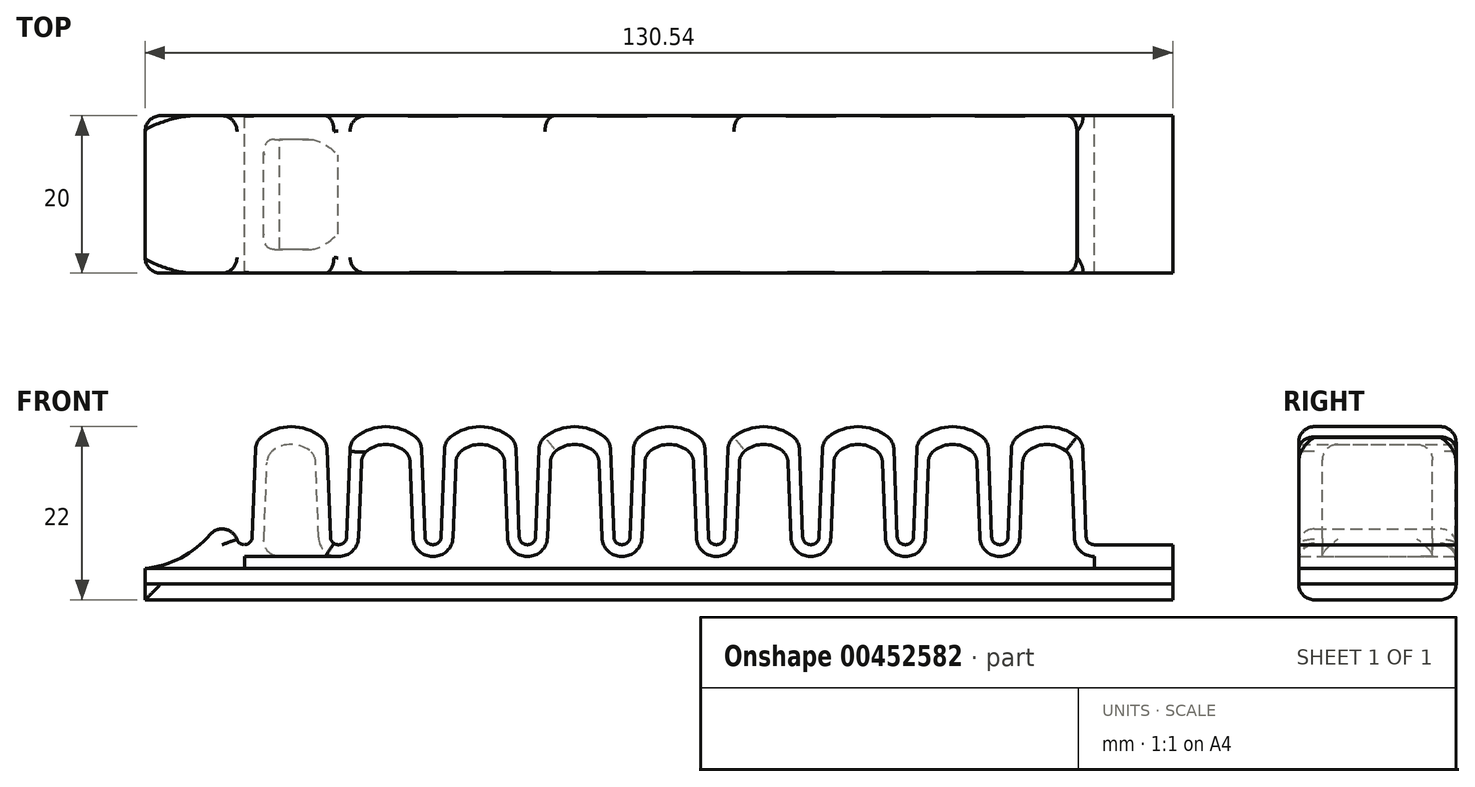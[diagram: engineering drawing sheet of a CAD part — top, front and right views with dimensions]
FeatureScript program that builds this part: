
annotation { "Feature Type Name" : "Feature", "Feature Type Description" : "" }
export const myFeature = defineFeature(function(context is Context, id is Id, definition is map)
    precondition{}
    {
        {
            assignVariable(context, id + "F0", {"name" : "vacChamberL", "anyValue" : 20});
        }
        {
            assignVariable(context, id + "F1", {"name" : "vacChamberFillet", "anyValue" : 1});
        }
        {
            assignVariable(context, id + "F2", {"name" : "vacChamberInterChamberWallThickness", "anyValue" : 1.5});
        }
        {
            var Q0;
            Q0=qCreatedBy(makeId("Front.planeOp"),FACE);
            var sketch = newSketch(context, id + "F3", { "sketchPlane" : qUnion([Q0])});
            skLineSegment(sketch, "E0", {"start": v(0, 0) * mm, "end": v(0, 5) * mm, "construction": true});
            skLineSegment(sketch, "E1", {"start": v(0, 0) * mm, "end": v(5, 0) * mm, "construction": true});
            skLineSegment(sketch, "E2", {"start": v(5, 0) * mm, "end": v(5, 20) * mm, "construction": true});
            skLineSegment(sketch, "E3", {"start": v(5, 0) * mm, "end": v(0.5, 0) * mm, "construction": true});
            skLineSegment(sketch, "E4", {"start": v(0.5, 0) * mm, "end": v(0.5, 18) * mm, "construction": true});
            skLineSegment(sketch, "E5", {"start": v(0.04, 5.96) * mm, "end": v(0.47, 17.2) * mm});
            skLineSegment(sketch, "E6", {"start": v(-0.96, 5) * mm, "end": v(-1, 5) * mm});
            skPoint(sketch, "E7.visualSharp", {"position": v(0, 5) * mm});
            skArc(sketch, "E7.filletArc", {"start": v(-0.96, 5) * mm, "mid": v(-0.27, 5.28) * mm, "end": v(0.04, 5.96) * mm});
            skArc(sketch, "E8.MirrorCS", {"start": v(10.96, 5) * mm, "mid": v(10.27, 5.28) * mm, "end": v(9.96, 5.96) * mm});
            skLineSegment(sketch, "E9.MirrorCS", {"start": v(9.96, 5.96) * mm, "end": v(9.53, 17.2) * mm});
            skArc(sketch, "E10", {"start": v(8.78, 18.68) * mm, "mid": v(5, 20) * mm, "end": v(1.22, 18.68) * mm});
            skPoint(sketch, "E11.visualSharp", {"position": v(0.5, 18) * mm});
            skArc(sketch, "E11.filletArc", {"start": v(1.22, 18.68) * mm, "mid": v(0.68, 18.02) * mm, "end": v(0.47, 17.2) * mm});
            skPoint(sketch, "E12.visualSharp", {"position": v(9.5, 18) * mm});
            skArc(sketch, "E12.filletArc", {"start": v(9.53, 17.2) * mm, "mid": v(9.32, 18.02) * mm, "end": v(8.78, 18.68) * mm});
            skSolve(sketch);
        }
        {
            var Q0;
            Q0=qCreatedBy(makeId("Front.planeOp"),FACE);
            var sketch = newSketch(context, id + "F4", { "sketchPlane" : qUnion([Q0])});
            skLineSegment(sketch, "E13.0", {"start": v(0.04, 5.96) * mm, "end": v(0.47, 17.2) * mm});
            skArc(sketch, "E13.1", {"start": v(-0.96, 5) * mm, "mid": v(-0.27, 5.28) * mm, "end": v(0.04, 5.96) * mm});
            skArc(sketch, "E13.2", {"start": v(8.78, 18.68) * mm, "mid": v(5, 20) * mm, "end": v(1.22, 18.68) * mm});
            skArc(sketch, "E13.3", {"start": v(1.22, 18.68) * mm, "mid": v(0.68, 18.02) * mm, "end": v(0.47, 17.2) * mm});
            skArc(sketch, "E13.4", {"start": v(9.53, 17.2) * mm, "mid": v(9.32, 18.02) * mm, "end": v(8.78, 18.68) * mm});
            skLineSegment(sketch, "E13.5", {"start": v(9.96, 5.96) * mm, "end": v(9.53, 17.2) * mm});
            skArc(sketch, "E13.6", {"start": v(10.96, 5) * mm, "mid": v(10.27, 5.28) * mm, "end": v(9.96, 5.96) * mm});
            skArc(sketch, "E14.1.0.0", {"start": v(22.96, 5) * mm, "mid": v(22.27, 5.28) * mm, "end": v(21.96, 5.96) * mm});
            skArc(sketch, "E14.1.0.1", {"start": v(20.78, 18.68) * mm, "mid": v(17, 20) * mm, "end": v(13.22, 18.68) * mm});
            skArc(sketch, "E14.1.0.2", {"start": v(11.04, 5) * mm, "mid": v(11.73, 5.28) * mm, "end": v(12.04, 5.96) * mm});
            skLineSegment(sketch, "E14.1.0.3", {"start": v(12.04, 5.96) * mm, "end": v(12.47, 17.2) * mm});
            skLineSegment(sketch, "E14.1.0.4", {"start": v(21.96, 5.96) * mm, "end": v(21.53, 17.2) * mm});
            skArc(sketch, "E14.1.0.5", {"start": v(21.53, 17.2) * mm, "mid": v(21.32, 18.02) * mm, "end": v(20.78, 18.68) * mm});
            skArc(sketch, "E14.1.0.6", {"start": v(13.22, 18.68) * mm, "mid": v(12.68, 18.02) * mm, "end": v(12.47, 17.2) * mm});
            skArc(sketch, "E14.2.0.0", {"start": v(34.96, 5) * mm, "mid": v(34.27, 5.28) * mm, "end": v(33.96, 5.96) * mm});
            skArc(sketch, "E14.2.0.1", {"start": v(32.78, 18.68) * mm, "mid": v(29, 20) * mm, "end": v(25.22, 18.68) * mm});
            skArc(sketch, "E14.2.0.2", {"start": v(23.04, 5) * mm, "mid": v(23.73, 5.28) * mm, "end": v(24.04, 5.96) * mm});
            skLineSegment(sketch, "E14.2.0.3", {"start": v(24.04, 5.96) * mm, "end": v(24.47, 17.2) * mm});
            skLineSegment(sketch, "E14.2.0.4", {"start": v(33.96, 5.96) * mm, "end": v(33.53, 17.2) * mm});
            skArc(sketch, "E14.2.0.5", {"start": v(33.53, 17.2) * mm, "mid": v(33.32, 18.02) * mm, "end": v(32.78, 18.68) * mm});
            skArc(sketch, "E14.2.0.6", {"start": v(25.22, 18.68) * mm, "mid": v(24.68, 18.02) * mm, "end": v(24.47, 17.2) * mm});
            skArc(sketch, "E14.3.0.0", {"start": v(46.96, 5) * mm, "mid": v(46.27, 5.28) * mm, "end": v(45.96, 5.96) * mm});
            skArc(sketch, "E14.3.0.1", {"start": v(44.78, 18.68) * mm, "mid": v(41, 20) * mm, "end": v(37.22, 18.68) * mm});
            skArc(sketch, "E14.3.0.2", {"start": v(35.04, 5) * mm, "mid": v(35.73, 5.28) * mm, "end": v(36.04, 5.96) * mm});
            skLineSegment(sketch, "E14.3.0.3", {"start": v(36.04, 5.96) * mm, "end": v(36.47, 17.2) * mm});
            skLineSegment(sketch, "E14.3.0.4", {"start": v(45.96, 5.96) * mm, "end": v(45.53, 17.2) * mm});
            skArc(sketch, "E14.3.0.5", {"start": v(45.53, 17.2) * mm, "mid": v(45.32, 18.02) * mm, "end": v(44.78, 18.68) * mm});
            skArc(sketch, "E14.3.0.6", {"start": v(37.22, 18.68) * mm, "mid": v(36.68, 18.02) * mm, "end": v(36.47, 17.2) * mm});
            skArc(sketch, "E14.4.0.0", {"start": v(58.96, 5) * mm, "mid": v(58.27, 5.28) * mm, "end": v(57.96, 5.96) * mm});
            skArc(sketch, "E14.4.0.1", {"start": v(56.78, 18.68) * mm, "mid": v(53, 20) * mm, "end": v(49.22, 18.68) * mm});
            skArc(sketch, "E14.4.0.2", {"start": v(47.04, 5) * mm, "mid": v(47.73, 5.28) * mm, "end": v(48.04, 5.96) * mm});
            skLineSegment(sketch, "E14.4.0.3", {"start": v(48.04, 5.96) * mm, "end": v(48.47, 17.2) * mm});
            skLineSegment(sketch, "E14.4.0.4", {"start": v(57.96, 5.96) * mm, "end": v(57.53, 17.2) * mm});
            skArc(sketch, "E14.4.0.5", {"start": v(57.53, 17.2) * mm, "mid": v(57.32, 18.02) * mm, "end": v(56.78, 18.68) * mm});
            skArc(sketch, "E14.4.0.6", {"start": v(49.22, 18.68) * mm, "mid": v(48.68, 18.02) * mm, "end": v(48.47, 17.2) * mm});
            skArc(sketch, "E14.5.0.0", {"start": v(70.96, 5) * mm, "mid": v(70.27, 5.28) * mm, "end": v(69.96, 5.96) * mm});
            skArc(sketch, "E14.5.0.1", {"start": v(68.78, 18.68) * mm, "mid": v(65, 20) * mm, "end": v(61.22, 18.68) * mm});
            skArc(sketch, "E14.5.0.2", {"start": v(59.04, 5) * mm, "mid": v(59.73, 5.28) * mm, "end": v(60.04, 5.96) * mm});
            skLineSegment(sketch, "E14.5.0.3", {"start": v(60.04, 5.96) * mm, "end": v(60.47, 17.2) * mm});
            skLineSegment(sketch, "E14.5.0.4", {"start": v(69.96, 5.96) * mm, "end": v(69.53, 17.2) * mm});
            skArc(sketch, "E14.5.0.5", {"start": v(69.53, 17.2) * mm, "mid": v(69.32, 18.02) * mm, "end": v(68.78, 18.68) * mm});
            skArc(sketch, "E14.5.0.6", {"start": v(61.22, 18.68) * mm, "mid": v(60.68, 18.02) * mm, "end": v(60.47, 17.2) * mm});
            skArc(sketch, "E14.6.0.0", {"start": v(82.96, 5) * mm, "mid": v(82.27, 5.28) * mm, "end": v(81.96, 5.96) * mm});
            skArc(sketch, "E14.6.0.1", {"start": v(80.78, 18.68) * mm, "mid": v(77, 20) * mm, "end": v(73.22, 18.68) * mm});
            skArc(sketch, "E14.6.0.2", {"start": v(71.04, 5) * mm, "mid": v(71.73, 5.28) * mm, "end": v(72.04, 5.96) * mm});
            skLineSegment(sketch, "E14.6.0.3", {"start": v(72.04, 5.96) * mm, "end": v(72.47, 17.2) * mm});
            skLineSegment(sketch, "E14.6.0.4", {"start": v(81.96, 5.96) * mm, "end": v(81.53, 17.2) * mm});
            skArc(sketch, "E14.6.0.5", {"start": v(81.53, 17.2) * mm, "mid": v(81.32, 18.02) * mm, "end": v(80.78, 18.68) * mm});
            skArc(sketch, "E14.6.0.6", {"start": v(73.22, 18.68) * mm, "mid": v(72.68, 18.02) * mm, "end": v(72.47, 17.2) * mm});
            skArc(sketch, "E14.7.0.0", {"start": v(94.96, 5) * mm, "mid": v(94.27, 5.28) * mm, "end": v(93.96, 5.96) * mm});
            skArc(sketch, "E14.7.0.1", {"start": v(92.78, 18.68) * mm, "mid": v(89, 20) * mm, "end": v(85.22, 18.68) * mm});
            skArc(sketch, "E14.7.0.2", {"start": v(83.04, 5) * mm, "mid": v(83.73, 5.28) * mm, "end": v(84.04, 5.96) * mm});
            skLineSegment(sketch, "E14.7.0.3", {"start": v(84.04, 5.96) * mm, "end": v(84.47, 17.2) * mm});
            skLineSegment(sketch, "E14.7.0.4", {"start": v(93.96, 5.96) * mm, "end": v(93.53, 17.2) * mm});
            skArc(sketch, "E14.7.0.5", {"start": v(93.53, 17.2) * mm, "mid": v(93.32, 18.02) * mm, "end": v(92.78, 18.68) * mm});
            skArc(sketch, "E14.7.0.6", {"start": v(85.22, 18.68) * mm, "mid": v(84.68, 18.02) * mm, "end": v(84.47, 17.2) * mm});
            skLineSegment(sketch, "E14.direction1", {"start": v(-0.96, 5) * mm, "end": v(11.04, 5) * mm, "construction": true});
            skLineSegment(sketch, "E15", {"start": v(-0.96, 5) * mm, "end": v(-0.96, 2.72) * mm, "construction": true});
            skArc(sketch, "E16.MirrorCS", {"start": v(-0.96, 5) * mm, "mid": v(-1.66, 5.28) * mm, "end": v(-1.96, 5.96) * mm});
            skLineSegment(sketch, "E17", {"start": v(-1.96, 5.96) * mm, "end": v(-2.08, 8.96) * mm});
            skLineSegment(sketch, "E18", {"start": v(-2.08, 8.96) * mm, "end": v(-3.58, 8.96) * mm});
            skLineSegment(sketch, "E19", {"start": v(-3.58, 0) * mm, "end": v(-13.58, 0) * mm, "construction": true});
            skLineSegment(sketch, "E20", {"start": v(-3.58, 0) * mm, "end": v(-5.58, 0) * mm, "construction": true});
            skLineSegment(sketch, "E21", {"start": v(-5.58, 0) * mm, "end": v(-5.58, 6) * mm, "construction": true});
            skLineSegment(sketch, "E22", {"start": v(10.96, 5) * mm, "end": v(11.04, 5) * mm});
            skLineSegment(sketch, "E23", {"start": v(22.96, 5) * mm, "end": v(23.04, 5) * mm});
            skLineSegment(sketch, "E24", {"start": v(34.96, 5) * mm, "end": v(35.04, 5) * mm});
            skLineSegment(sketch, "E25", {"start": v(46.96, 5) * mm, "end": v(47.04, 5) * mm});
            skLineSegment(sketch, "E26", {"start": v(58.96, 5) * mm, "end": v(59.04, 5) * mm});
            skLineSegment(sketch, "E27", {"start": v(70.96, 5) * mm, "end": v(71.04, 5) * mm});
            skLineSegment(sketch, "E28", {"start": v(82.96, 5) * mm, "end": v(83.04, 5) * mm});
            skArc(sketch, "E29.0.8.0", {"start": v(106.96, 5) * mm, "mid": v(106.27, 5.28) * mm, "end": v(105.96, 5.96) * mm});
            skArc(sketch, "E29.4.8.0", {"start": v(104.78, 18.68) * mm, "mid": v(101, 20) * mm, "end": v(97.22, 18.68) * mm});
            skArc(sketch, "E29.8.8.0", {"start": v(95.04, 5) * mm, "mid": v(95.73, 5.28) * mm, "end": v(96.04, 5.96) * mm});
            skLineSegment(sketch, "E29.12.8.0", {"start": v(96.04, 5.96) * mm, "end": v(96.47, 17.2) * mm});
            skLineSegment(sketch, "E29.15.8.0", {"start": v(105.96, 5.96) * mm, "end": v(105.53, 17.2) * mm});
            skArc(sketch, "E29.18.8.0", {"start": v(105.53, 17.2) * mm, "mid": v(105.32, 18.02) * mm, "end": v(104.78, 18.68) * mm});
            skArc(sketch, "E29.22.8.0", {"start": v(97.22, 18.68) * mm, "mid": v(96.68, 18.02) * mm, "end": v(96.47, 17.2) * mm});
            skLineSegment(sketch, "E30", {"start": v(94.96, 5) * mm, "end": v(95.04, 5) * mm});
            skLineSegment(sketch, "E31", {"start": v(106.96, 5) * mm, "end": v(116.96, 5) * mm});
            skArc(sketch, "E32.0", {"start": v(-0.96, 3.5) * mm, "mid": v(0.77, 4.2) * mm, "end": v(1.54, 5.9) * mm});
            skLineSegment(sketch, "E32.1", {"start": v(1.54, 5.9) * mm, "end": v(1.9, 15.46) * mm});
            skLineSegment(sketch, "E32.4", {"start": v(10.96, 3.5) * mm, "end": v(11.04, 3.5) * mm});
            skArc(sketch, "E32.5", {"start": v(10.96, 3.5) * mm, "mid": v(9.23, 4.2) * mm, "end": v(8.46, 5.9) * mm});
            skLineSegment(sketch, "E32.6", {"start": v(8.46, 5.9) * mm, "end": v(8.1, 15.46) * mm});
            skArc(sketch, "E33.0", {"start": v(7.31, 16.97) * mm, "mid": v(5, 17.75) * mm, "end": v(2.69, 16.97) * mm});
            skPoint(sketch, "E34.visualSharp", {"position": v(1.93, 16.2) * mm});
            skArc(sketch, "E34.filletArc", {"start": v(2.69, 16.97) * mm, "mid": v(2.13, 16.3) * mm, "end": v(1.9, 15.46) * mm});
            skPoint(sketch, "E35.visualSharp", {"position": v(8.07, 16.2) * mm});
            skArc(sketch, "E35.filletArc", {"start": v(8.1, 15.46) * mm, "mid": v(7.87, 16.3) * mm, "end": v(7.31, 16.97) * mm});
            skArc(sketch, "E36.1.0.0", {"start": v(22.96, 3.5) * mm, "mid": v(21.23, 4.2) * mm, "end": v(20.46, 5.9) * mm});
            skLineSegment(sketch, "E36.1.0.1", {"start": v(22.96, 3.5) * mm, "end": v(23.04, 3.5) * mm});
            skLineSegment(sketch, "E36.1.0.2", {"start": v(20.46, 5.9) * mm, "end": v(20.1, 15.46) * mm});
            skArc(sketch, "E36.1.0.3", {"start": v(20.1, 15.46) * mm, "mid": v(19.87, 16.3) * mm, "end": v(19.31, 16.97) * mm});
            skArc(sketch, "E36.1.0.4", {"start": v(19.31, 16.97) * mm, "mid": v(17, 17.75) * mm, "end": v(14.69, 16.97) * mm});
            skArc(sketch, "E36.1.0.5", {"start": v(14.69, 16.97) * mm, "mid": v(14.13, 16.3) * mm, "end": v(13.9, 15.46) * mm});
            skLineSegment(sketch, "E36.1.0.6", {"start": v(13.54, 5.9) * mm, "end": v(13.9, 15.46) * mm});
            skArc(sketch, "E36.1.0.7", {"start": v(11.04, 3.5) * mm, "mid": v(12.77, 4.2) * mm, "end": v(13.54, 5.9) * mm});
            skArc(sketch, "E36.2.0.0", {"start": v(34.96, 3.5) * mm, "mid": v(33.23, 4.2) * mm, "end": v(32.46, 5.9) * mm});
            skLineSegment(sketch, "E36.2.0.1", {"start": v(34.96, 3.5) * mm, "end": v(35.04, 3.5) * mm});
            skLineSegment(sketch, "E36.2.0.2", {"start": v(32.46, 5.9) * mm, "end": v(32.1, 15.46) * mm});
            skArc(sketch, "E36.2.0.3", {"start": v(32.1, 15.46) * mm, "mid": v(31.87, 16.3) * mm, "end": v(31.31, 16.97) * mm});
            skArc(sketch, "E36.2.0.4", {"start": v(31.31, 16.97) * mm, "mid": v(29, 17.75) * mm, "end": v(26.69, 16.97) * mm});
            skArc(sketch, "E36.2.0.5", {"start": v(26.69, 16.97) * mm, "mid": v(26.13, 16.3) * mm, "end": v(25.9, 15.46) * mm});
            skLineSegment(sketch, "E36.2.0.6", {"start": v(25.54, 5.9) * mm, "end": v(25.9, 15.46) * mm});
            skArc(sketch, "E36.2.0.7", {"start": v(23.04, 3.5) * mm, "mid": v(24.77, 4.2) * mm, "end": v(25.54, 5.9) * mm});
            skArc(sketch, "E36.3.0.0", {"start": v(46.96, 3.5) * mm, "mid": v(45.23, 4.2) * mm, "end": v(44.46, 5.9) * mm});
            skLineSegment(sketch, "E36.3.0.1", {"start": v(46.96, 3.5) * mm, "end": v(47.04, 3.5) * mm});
            skLineSegment(sketch, "E36.3.0.2", {"start": v(44.46, 5.9) * mm, "end": v(44.1, 15.46) * mm});
            skArc(sketch, "E36.3.0.3", {"start": v(44.1, 15.46) * mm, "mid": v(43.87, 16.3) * mm, "end": v(43.31, 16.97) * mm});
            skArc(sketch, "E36.3.0.4", {"start": v(43.31, 16.97) * mm, "mid": v(41, 17.75) * mm, "end": v(38.69, 16.97) * mm});
            skArc(sketch, "E36.3.0.5", {"start": v(38.69, 16.97) * mm, "mid": v(38.13, 16.3) * mm, "end": v(37.9, 15.46) * mm});
            skLineSegment(sketch, "E36.3.0.6", {"start": v(37.54, 5.9) * mm, "end": v(37.9, 15.46) * mm});
            skArc(sketch, "E36.3.0.7", {"start": v(35.04, 3.5) * mm, "mid": v(36.77, 4.2) * mm, "end": v(37.54, 5.9) * mm});
            skArc(sketch, "E36.4.0.0", {"start": v(58.96, 3.5) * mm, "mid": v(57.23, 4.2) * mm, "end": v(56.46, 5.9) * mm});
            skLineSegment(sketch, "E36.4.0.1", {"start": v(58.96, 3.5) * mm, "end": v(59.04, 3.5) * mm});
            skLineSegment(sketch, "E36.4.0.2", {"start": v(56.46, 5.9) * mm, "end": v(56.1, 15.46) * mm});
            skArc(sketch, "E36.4.0.3", {"start": v(56.1, 15.46) * mm, "mid": v(55.87, 16.3) * mm, "end": v(55.31, 16.97) * mm});
            skArc(sketch, "E36.4.0.4", {"start": v(55.31, 16.97) * mm, "mid": v(53, 17.75) * mm, "end": v(50.69, 16.97) * mm});
            skArc(sketch, "E36.4.0.5", {"start": v(50.69, 16.97) * mm, "mid": v(50.13, 16.3) * mm, "end": v(49.9, 15.46) * mm});
            skLineSegment(sketch, "E36.4.0.6", {"start": v(49.54, 5.9) * mm, "end": v(49.9, 15.46) * mm});
            skArc(sketch, "E36.4.0.7", {"start": v(47.04, 3.5) * mm, "mid": v(48.77, 4.2) * mm, "end": v(49.54, 5.9) * mm});
            skArc(sketch, "E36.5.0.0", {"start": v(70.96, 3.5) * mm, "mid": v(69.23, 4.2) * mm, "end": v(68.46, 5.9) * mm});
            skLineSegment(sketch, "E36.5.0.1", {"start": v(70.96, 3.5) * mm, "end": v(71.04, 3.5) * mm});
            skLineSegment(sketch, "E36.5.0.2", {"start": v(68.46, 5.9) * mm, "end": v(68.1, 15.46) * mm});
            skArc(sketch, "E36.5.0.3", {"start": v(68.1, 15.46) * mm, "mid": v(67.87, 16.3) * mm, "end": v(67.31, 16.97) * mm});
            skArc(sketch, "E36.5.0.4", {"start": v(67.31, 16.97) * mm, "mid": v(65, 17.75) * mm, "end": v(62.69, 16.97) * mm});
            skArc(sketch, "E36.5.0.5", {"start": v(62.69, 16.97) * mm, "mid": v(62.13, 16.3) * mm, "end": v(61.9, 15.46) * mm});
            skLineSegment(sketch, "E36.5.0.6", {"start": v(61.54, 5.9) * mm, "end": v(61.9, 15.46) * mm});
            skArc(sketch, "E36.5.0.7", {"start": v(59.04, 3.5) * mm, "mid": v(60.77, 4.2) * mm, "end": v(61.54, 5.9) * mm});
            skArc(sketch, "E36.6.0.0", {"start": v(82.96, 3.5) * mm, "mid": v(81.23, 4.2) * mm, "end": v(80.46, 5.9) * mm});
            skLineSegment(sketch, "E36.6.0.1", {"start": v(82.96, 3.5) * mm, "end": v(83.04, 3.5) * mm});
            skLineSegment(sketch, "E36.6.0.2", {"start": v(80.46, 5.9) * mm, "end": v(80.1, 15.46) * mm});
            skArc(sketch, "E36.6.0.3", {"start": v(80.1, 15.46) * mm, "mid": v(79.87, 16.3) * mm, "end": v(79.31, 16.97) * mm});
            skArc(sketch, "E36.6.0.4", {"start": v(79.31, 16.97) * mm, "mid": v(77, 17.75) * mm, "end": v(74.69, 16.97) * mm});
            skArc(sketch, "E36.6.0.5", {"start": v(74.69, 16.97) * mm, "mid": v(74.13, 16.3) * mm, "end": v(73.9, 15.46) * mm});
            skLineSegment(sketch, "E36.6.0.6", {"start": v(73.54, 5.9) * mm, "end": v(73.9, 15.46) * mm});
            skArc(sketch, "E36.6.0.7", {"start": v(71.04, 3.5) * mm, "mid": v(72.77, 4.2) * mm, "end": v(73.54, 5.9) * mm});
            skArc(sketch, "E36.7.0.0", {"start": v(94.96, 3.5) * mm, "mid": v(93.23, 4.2) * mm, "end": v(92.46, 5.9) * mm});
            skLineSegment(sketch, "E36.7.0.1", {"start": v(94.96, 3.5) * mm, "end": v(95.04, 3.5) * mm});
            skLineSegment(sketch, "E36.7.0.2", {"start": v(92.46, 5.9) * mm, "end": v(92.1, 15.46) * mm});
            skArc(sketch, "E36.7.0.3", {"start": v(92.1, 15.46) * mm, "mid": v(91.87, 16.3) * mm, "end": v(91.31, 16.97) * mm});
            skArc(sketch, "E36.7.0.4", {"start": v(91.31, 16.97) * mm, "mid": v(89, 17.75) * mm, "end": v(86.69, 16.97) * mm});
            skArc(sketch, "E36.7.0.5", {"start": v(86.69, 16.97) * mm, "mid": v(86.13, 16.3) * mm, "end": v(85.9, 15.46) * mm});
            skLineSegment(sketch, "E36.7.0.6", {"start": v(85.54, 5.9) * mm, "end": v(85.9, 15.46) * mm});
            skArc(sketch, "E36.7.0.7", {"start": v(83.04, 3.5) * mm, "mid": v(84.77, 4.2) * mm, "end": v(85.54, 5.9) * mm});
            skArc(sketch, "E36.8.0.0", {"start": v(106.96, 3.5) * mm, "mid": v(105.23, 4.2) * mm, "end": v(104.46, 5.9) * mm});
            skLineSegment(sketch, "E36.8.0.1", {"start": v(106.96, 3.5) * mm, "end": v(107.04, 3.5) * mm});
            skLineSegment(sketch, "E36.8.0.2", {"start": v(104.46, 5.9) * mm, "end": v(104.1, 15.46) * mm});
            skArc(sketch, "E36.8.0.3", {"start": v(104.1, 15.46) * mm, "mid": v(103.87, 16.3) * mm, "end": v(103.31, 16.97) * mm});
            skArc(sketch, "E36.8.0.4", {"start": v(103.31, 16.97) * mm, "mid": v(101, 17.75) * mm, "end": v(98.69, 16.97) * mm});
            skArc(sketch, "E36.8.0.5", {"start": v(98.69, 16.97) * mm, "mid": v(98.13, 16.3) * mm, "end": v(97.9, 15.46) * mm});
            skLineSegment(sketch, "E36.8.0.6", {"start": v(97.54, 5.9) * mm, "end": v(97.9, 15.46) * mm});
            skArc(sketch, "E36.8.0.7", {"start": v(95.04, 3.5) * mm, "mid": v(96.77, 4.2) * mm, "end": v(97.54, 5.9) * mm});
            skLineSegment(sketch, "E36.direction1", {"start": v(-0.96, 3.5) * mm, "end": v(11.04, 3.5) * mm, "construction": true});
            skLineSegment(sketch, "E37", {"start": v(107.04, 3.5) * mm, "end": v(116.96, 3.5) * mm});
            skLineSegment(sketch, "E38", {"start": v(-13.58, 0) * mm, "end": v(116.96, 0) * mm});
            skLineSegment(sketch, "E39", {"start": v(116.96, 0) * mm, "end": v(116.96, 2) * mm});
            skLineSegment(sketch, "E40", {"start": v(116.96, 2) * mm, "end": v(-0.96, 2) * mm});
            skLineSegment(sketch, "E41", {"start": v(-0.96, 2) * mm, "end": v(-0.96, 3.5) * mm});
            skLineSegment(sketch, "E42", {"start": v(116.96, 3.5) * mm, "end": v(116.96, 5) * mm});
            skLineSegment(sketch, "E43", {"start": v(116.96, 3.5) * mm, "end": v(116.96, 2) * mm});
            skLineSegment(sketch, "E44", {"start": v(116.96, 0) * mm, "end": v(116.96, -2) * mm});
            skLineSegment(sketch, "E45", {"start": v(116.96, -2) * mm, "end": v(-13.58, -2) * mm});
            skLineSegment(sketch, "E46", {"start": v(-13.58, -2) * mm, "end": v(-13.58, 0) * mm});
            skLineSegment(sketch, "E47", {"start": v(-13.58, 0) * mm, "end": v(-13.58, 2) * mm});
            skLineSegment(sketch, "E48", {"start": v(-13.58, 2) * mm, "end": v(-0.96, 2) * mm});
            skArc(sketch, "E49", {"start": v(-13.58, 2) * mm, "mid": v(-7.66, 4.17) * mm, "end": v(-3.58, 8.96) * mm});
            skLineSegment(sketch, "E50", {"start": v(107.04, 3.5) * mm, "end": v(-0.96, 3.5) * mm});
            skLineSegment(sketch, "E51.0", {"start": v(109.37, 6.5) * mm, "end": v(116.96, 6.5) * mm});
            skLineSegment(sketch, "E51.1", {"start": v(107.37, 8.42) * mm, "end": v(107.1, 15.45) * mm});
            skLineSegment(sketch, "E52", {"start": v(116.96, 6.5) * mm, "end": v(116.96, 5) * mm});
            skLineSegment(sketch, "E53", {"start": v(106.02, 17.64) * mm, "end": v(104.78, 18.68) * mm});
            skPoint(sketch, "E54.visualSharp", {"position": v(107.44, 6.5) * mm});
            skArc(sketch, "E54.filletArc", {"start": v(107.37, 8.42) * mm, "mid": v(107.98, 7.06) * mm, "end": v(109.37, 6.5) * mm});
            skPoint(sketch, "E55.visualSharp", {"position": v(107.05, 16.79) * mm});
            skArc(sketch, "E55.filletArc", {"start": v(107.1, 15.45) * mm, "mid": v(106.8, 16.66) * mm, "end": v(106.02, 17.64) * mm});
            skLineSegment(sketch, "E56", {"start": v(107.04, 3.5) * mm, "end": v(107.04, 2) * mm});
            skSolve(sketch);
        }
        {
            var Q0;
            Q0=makeQuery(id+"F4.imprint","IMPRINT",FACE,{"disambiguationData":[TD([[makeQuery(id+"F4.imprint","IMPRINT",EDGE,{"derivedFrom":sQuery(id+"F4.wireOp",EDGE,"E32.0")}),-1.0]])]});
            var Q1;
            {var subQ0=sQuery(id+"F4.wireOp",EDGE,"E36.1.0.0");Q1=makeQuery(id+"F4.imprint","IMPRINT",FACE,{"disambiguationData":[TD([[makeQuery(id+"F4.imprint","IMPRINT",EDGE,{"derivedFrom":subQ0}),1.0]])]});}
            var Q2;
            {var subQ0=sQuery(id+"F4.wireOp",EDGE,"E36.2.0.0");Q2=makeQuery(id+"F4.imprint","IMPRINT",FACE,{"disambiguationData":[TD([[makeQuery(id+"F4.imprint","IMPRINT",EDGE,{"derivedFrom":subQ0}),1.0]])]});}
            var Q3;
            {var subQ0=sQuery(id+"F4.wireOp",EDGE,"E36.3.0.0");Q3=makeQuery(id+"F4.imprint","IMPRINT",FACE,{"disambiguationData":[TD([[makeQuery(id+"F4.imprint","IMPRINT",EDGE,{"derivedFrom":subQ0}),1.0]])]});}
            var Q4;
            {var subQ1=sQuery(id+"F4.wireOp",EDGE,"E36.4.0.0");Q4=makeQuery(id+"F4.imprint","IMPRINT",FACE,{"disambiguationData":[TD([[makeQuery(id+"F4.imprint","IMPRINT",EDGE,{"derivedFrom":subQ1}),1.0]])]});}
            var Q5;
            {var subQ0=sQuery(id+"F4.wireOp",EDGE,"E36.5.0.0");Q5=makeQuery(id+"F4.imprint","IMPRINT",FACE,{"disambiguationData":[TD([[makeQuery(id+"F4.imprint","IMPRINT",EDGE,{"derivedFrom":subQ0}),1.0]])]});}
            var Q6;
            {var subQ0=sQuery(id+"F4.wireOp",EDGE,"E36.6.0.0");Q6=makeQuery(id+"F4.imprint","IMPRINT",FACE,{"disambiguationData":[TD([[makeQuery(id+"F4.imprint","IMPRINT",EDGE,{"derivedFrom":subQ0}),1.0]])]});}
            var Q7;
            {var subQ0=sQuery(id+"F4.wireOp",EDGE,"E36.7.0.0");Q7=makeQuery(id+"F4.imprint","IMPRINT",FACE,{"disambiguationData":[TD([[makeQuery(id+"F4.imprint","IMPRINT",EDGE,{"derivedFrom":subQ0}),1.0]])]});}
            var Q8;
            {var subQ0=sQuery(id+"F4.wireOp",EDGE,"E36.8.0.0");Q8=makeQuery(id+"F4.imprint","IMPRINT",FACE,{"disambiguationData":[TD([[makeQuery(id+"F4.imprint","IMPRINT",EDGE,{"derivedFrom":subQ0}),1.0]])]});}
            var Q9;
            {var subQ10=sQuery(id+"F4.wireOp",EDGE,"E41");Q9=makeQuery(id+"F4.imprint","IMPRINT",FACE,{"disambiguationData":[TD([[makeQuery(id+"F4.imprint","IMPRINT",EDGE,{"derivedFrom":subQ10}),-1.0]])]});}
            extrude(context, id + "F5", {"entities" : qUnion([Q0, Q1, Q2, Q3, Q4, Q5, Q6, Q7, Q8, Q9]), "depth" : (getVariable(context, 'vacChamberL') - 4 * getVariable(context, 'vacChamberInterChamberWallThickness')) * mm, "symmetric" : true});
        }
        {
            var Q0;
            Q0=makeQuery(id+"F5.opExtrude","CAP_EDGE",EDGE,{"disambiguationData":[OSD([sQuery(id+"F4.wireOp",EDGE,"E33.0")])],"isStart":false});
            var Q1;
            Q1=makeQuery(id+"F5.opExtrude","CAP_EDGE",EDGE,{"disambiguationData":[OSD([sQuery(id+"F4.wireOp",EDGE,"E33.0")])],"isStart":true});
            var Q2;
            Q2=makeQuery(id+"F5.opExtrude","SWEPT_EDGE",EDGE,{"disambiguationData":[OSD([sQuery(id+"F4.wireOp",EDGE,"E32.0"),sQuery(id+"F4.wireOp",EDGE,"E41")])]});
            fillet(context, id + "F6", {"entities" : qUnion([Q0, Q1, Q2]), "radius" : (getVariable(context, 'vacChamberFillet') * 2) * mm, "tangentPropagation" : true, "allowEdgeOverflow" : false});
        }
        {
            var Q0;
            Q0=makeQuery(id+"F4.imprint","IMPRINT",FACE,{"disambiguationData":[TD([[makeQuery(id+"F4.imprint","IMPRINT",EDGE,{"derivedFrom":sQuery(id+"F4.wireOp",EDGE,"E13.0")}),-1.0]])]});
            var Q1;
            Q1=makeQuery(id+"F4.imprint","IMPRINT",FACE,{"disambiguationData":[TD([[makeQuery(id+"F4.imprint","IMPRINT",EDGE,{"derivedFrom":sQuery(id+"F4.wireOp",EDGE,"E32.0")}),-1.0]])]});
            var Q2;
            {var subQ6=sQuery(id+"F4.wireOp",EDGE,"E37");Q2=makeQuery(id+"F4.imprint","IMPRINT",FACE,{"disambiguationData":[TD([[makeQuery(id+"F4.imprint","IMPRINT",EDGE,{"derivedFrom":subQ6}),-1.0]])]});}
            var Q3;
            {var subQ0=sQuery(id+"F4.wireOp",EDGE,"E36.1.0.0");Q3=makeQuery(id+"F4.imprint","IMPRINT",FACE,{"disambiguationData":[TD([[makeQuery(id+"F4.imprint","IMPRINT",EDGE,{"derivedFrom":subQ0}),1.0]])]});}
            var Q4;
            {var subQ0=sQuery(id+"F4.wireOp",EDGE,"E36.2.0.0");Q4=makeQuery(id+"F4.imprint","IMPRINT",FACE,{"disambiguationData":[TD([[makeQuery(id+"F4.imprint","IMPRINT",EDGE,{"derivedFrom":subQ0}),1.0]])]});}
            var Q5;
            {var subQ0=sQuery(id+"F4.wireOp",EDGE,"E36.3.0.0");Q5=makeQuery(id+"F4.imprint","IMPRINT",FACE,{"disambiguationData":[TD([[makeQuery(id+"F4.imprint","IMPRINT",EDGE,{"derivedFrom":subQ0}),1.0]])]});}
            var Q6;
            {var subQ1=sQuery(id+"F4.wireOp",EDGE,"E36.4.0.0");Q6=makeQuery(id+"F4.imprint","IMPRINT",FACE,{"disambiguationData":[TD([[makeQuery(id+"F4.imprint","IMPRINT",EDGE,{"derivedFrom":subQ1}),1.0]])]});}
            var Q7;
            {var subQ0=sQuery(id+"F4.wireOp",EDGE,"E36.5.0.0");Q7=makeQuery(id+"F4.imprint","IMPRINT",FACE,{"disambiguationData":[TD([[makeQuery(id+"F4.imprint","IMPRINT",EDGE,{"derivedFrom":subQ0}),1.0]])]});}
            var Q8;
            {var subQ0=sQuery(id+"F4.wireOp",EDGE,"E36.6.0.0");Q8=makeQuery(id+"F4.imprint","IMPRINT",FACE,{"disambiguationData":[TD([[makeQuery(id+"F4.imprint","IMPRINT",EDGE,{"derivedFrom":subQ0}),1.0]])]});}
            var Q9;
            {var subQ0=sQuery(id+"F4.wireOp",EDGE,"E36.7.0.0");Q9=makeQuery(id+"F4.imprint","IMPRINT",FACE,{"disambiguationData":[TD([[makeQuery(id+"F4.imprint","IMPRINT",EDGE,{"derivedFrom":subQ0}),1.0]])]});}
            var Q10;
            {var subQ0=sQuery(id+"F4.wireOp",EDGE,"E36.8.0.0");Q10=makeQuery(id+"F4.imprint","IMPRINT",FACE,{"disambiguationData":[TD([[makeQuery(id+"F4.imprint","IMPRINT",EDGE,{"derivedFrom":subQ0}),1.0]])]});}
            var Q11;
            Q11=makeQuery(id+"F4.imprint","IMPRINT",FACE,{"disambiguationData":[TD([[makeQuery(id+"F4.imprint","IMPRINT",EDGE,{"derivedFrom":sQuery(id+"F4.wireOp",EDGE,"E29.0.8.0")}),-1.0]])]});
            var Q12;
            {var subQ10=sQuery(id+"F4.wireOp",EDGE,"E41");Q12=makeQuery(id+"F4.imprint","IMPRINT",FACE,{"disambiguationData":[TD([[makeQuery(id+"F4.imprint","IMPRINT",EDGE,{"derivedFrom":subQ10}),-1.0]])]});}
            extrude(context, id + "F7", {"entities" : qUnion([Q0, Q1, Q2, Q3, Q4, Q5, Q6, Q7, Q8, Q9, Q10, Q11, Q12]), "depth" : (getVariable(context, 'vacChamberL')) * mm, "symmetric" : true});
        }
        {
            var Q0;
            Q0=makeQuery(id+"F7.opExtrude","CAP_EDGE",EDGE,{"disambiguationData":[OSD([sQuery(id+"F4.wireOp",EDGE,"E13.2")])],"isStart":false});
            var Q1;
            Q1=makeQuery(id+"F7.opExtrude","CAP_EDGE",EDGE,{"disambiguationData":[OSD([sQuery(id+"F4.wireOp",EDGE,"E13.2")])],"isStart":true});
            var Q2;
            Q2=makeQuery(id+"F7.opExtrude","CAP_EDGE",EDGE,{"disambiguationData":[OSD([sQuery(id+"F4.wireOp",EDGE,"E51.1")])],"isStart":false});
            var Q3;
            Q3=makeQuery(id+"F7.opExtrude","CAP_EDGE",EDGE,{"disambiguationData":[OSD([sQuery(id+"F4.wireOp",EDGE,"E51.1")])],"isStart":true});
            fillet(context, id + "F8", {"entities" : qUnion([Q0, Q1, Q2, Q3]), "radius" : getVariable(context, 'vacChamberFillet') * 2 * mm, "tangentPropagation" : true, "allowEdgeOverflow" : false});
        }
        {
            var Q0;
            Q0=makeQuery(id+"F4.imprint","IMPRINT",FACE,{"disambiguationData":[TD([[makeQuery(id+"F4.imprint","IMPRINT",EDGE,{"derivedFrom":sQuery(id+"F4.wireOp",EDGE,"E38")}),1.0]])]});
            extrude(context, id + "F9", {"entities" : qUnion([Q0]), "depth" : (getVariable(context, 'vacChamberL')) * mm, "symmetric" : true});
        }
        {
            var Q0;
            Q0=makeQuery(id+"F4.imprint","IMPRINT",FACE,{"disambiguationData":[TD([[makeQuery(id+"F4.imprint","IMPRINT",EDGE,{"derivedFrom":sQuery(id+"F4.wireOp",EDGE,"E38")}),-1.0]])]});
            extrude(context, id + "F10", {"entities" : qUnion([Q0]), "depth" : (getVariable(context, 'vacChamberL')) * mm, "symmetric" : true});
        }
        {
            var Q0;
            Q0=makeQuery(id+"F5.opExtrude","SWEPT_BODY",BODY,{"disambiguationData":[OSD([sQuery(id+"F4.wireOp",EDGE,"E32.0"),sQuery(id+"F4.wireOp",EDGE,"E32.1"),sQuery(id+"F4.wireOp",EDGE,"E32.5"),sQuery(id+"F4.wireOp",EDGE,"E32.6"),sQuery(id+"F4.wireOp",EDGE,"E33.0"),sQuery(id+"F4.wireOp",EDGE,"E34.filletArc"),sQuery(id+"F4.wireOp",EDGE,"E35.filletArc"),sQuery(id+"F4.wireOp",EDGE,"E36.1.0.0"),sQuery(id+"F4.wireOp",EDGE,"E36.1.0.2"),sQuery(id+"F4.wireOp",EDGE,"E36.1.0.3"),sQuery(id+"F4.wireOp",EDGE,"E36.1.0.4"),sQuery(id+"F4.wireOp",EDGE,"E36.1.0.5"),sQuery(id+"F4.wireOp",EDGE,"E36.1.0.6"),sQuery(id+"F4.wireOp",EDGE,"E36.1.0.7"),sQuery(id+"F4.wireOp",EDGE,"E36.2.0.0"),sQuery(id+"F4.wireOp",EDGE,"E36.2.0.2"),sQuery(id+"F4.wireOp",EDGE,"E36.2.0.3"),sQuery(id+"F4.wireOp",EDGE,"E36.2.0.4"),sQuery(id+"F4.wireOp",EDGE,"E36.2.0.5"),sQuery(id+"F4.wireOp",EDGE,"E36.2.0.6"),sQuery(id+"F4.wireOp",EDGE,"E36.2.0.7"),sQuery(id+"F4.wireOp",EDGE,"E36.3.0.0"),sQuery(id+"F4.wireOp",EDGE,"E36.3.0.2"),sQuery(id+"F4.wireOp",EDGE,"E36.3.0.3"),sQuery(id+"F4.wireOp",EDGE,"E36.3.0.4"),sQuery(id+"F4.wireOp",EDGE,"E36.3.0.5"),sQuery(id+"F4.wireOp",EDGE,"E36.3.0.6"),sQuery(id+"F4.wireOp",EDGE,"E36.3.0.7"),sQuery(id+"F4.wireOp",EDGE,"E36.4.0.0"),sQuery(id+"F4.wireOp",EDGE,"E36.4.0.2"),sQuery(id+"F4.wireOp",EDGE,"E36.4.0.3"),sQuery(id+"F4.wireOp",EDGE,"E36.4.0.4"),sQuery(id+"F4.wireOp",EDGE,"E36.4.0.5"),sQuery(id+"F4.wireOp",EDGE,"E36.4.0.6"),sQuery(id+"F4.wireOp",EDGE,"E36.4.0.7"),sQuery(id+"F4.wireOp",EDGE,"E36.5.0.0"),sQuery(id+"F4.wireOp",EDGE,"E36.5.0.2"),sQuery(id+"F4.wireOp",EDGE,"E36.5.0.3"),sQuery(id+"F4.wireOp",EDGE,"E36.5.0.4"),sQuery(id+"F4.wireOp",EDGE,"E36.5.0.5"),sQuery(id+"F4.wireOp",EDGE,"E36.5.0.6"),sQuery(id+"F4.wireOp",EDGE,"E36.5.0.7"),sQuery(id+"F4.wireOp",EDGE,"E36.6.0.0"),sQuery(id+"F4.wireOp",EDGE,"E36.6.0.2"),sQuery(id+"F4.wireOp",EDGE,"E36.6.0.3"),sQuery(id+"F4.wireOp",EDGE,"E36.6.0.4"),sQuery(id+"F4.wireOp",EDGE,"E36.6.0.5"),sQuery(id+"F4.wireOp",EDGE,"E36.6.0.6"),sQuery(id+"F4.wireOp",EDGE,"E36.6.0.7"),sQuery(id+"F4.wireOp",EDGE,"E36.7.0.0"),sQuery(id+"F4.wireOp",EDGE,"E36.7.0.2"),sQuery(id+"F4.wireOp",EDGE,"E36.7.0.3"),sQuery(id+"F4.wireOp",EDGE,"E36.7.0.4"),sQuery(id+"F4.wireOp",EDGE,"E36.7.0.5"),sQuery(id+"F4.wireOp",EDGE,"E36.7.0.6"),sQuery(id+"F4.wireOp",EDGE,"E36.7.0.7"),sQuery(id+"F4.wireOp",EDGE,"E36.8.0.0"),sQuery(id+"F4.wireOp",EDGE,"E36.8.0.2"),sQuery(id+"F4.wireOp",EDGE,"E36.8.0.3"),sQuery(id+"F4.wireOp",EDGE,"E36.8.0.4"),sQuery(id+"F4.wireOp",EDGE,"E36.8.0.5"),sQuery(id+"F4.wireOp",EDGE,"E36.8.0.6"),sQuery(id+"F4.wireOp",EDGE,"E36.8.0.7"),sQuery(id+"F4.wireOp",EDGE,"E37"),sQuery(id+"F4.wireOp",EDGE,"E40"),sQuery(id+"F4.wireOp",EDGE,"E41"),sQuery(id+"F4.wireOp",EDGE,"E43"),sQuery(id+"F4.wireOp",EDGE,"E50")])]});
            var Q1;
            Q1=makeQuery(id+"F7.opExtrude","SWEPT_BODY",BODY,{"disambiguationData":[OSD([sQuery(id+"F4.wireOp",EDGE,"E13.0"),sQuery(id+"F4.wireOp",EDGE,"E13.1"),sQuery(id+"F4.wireOp",EDGE,"E13.2"),sQuery(id+"F4.wireOp",EDGE,"E13.3"),sQuery(id+"F4.wireOp",EDGE,"E13.4"),sQuery(id+"F4.wireOp",EDGE,"E13.5"),sQuery(id+"F4.wireOp",EDGE,"E13.6"),sQuery(id+"F4.wireOp",EDGE,"E14.1.0.0"),sQuery(id+"F4.wireOp",EDGE,"E14.1.0.1"),sQuery(id+"F4.wireOp",EDGE,"E14.1.0.2"),sQuery(id+"F4.wireOp",EDGE,"E14.1.0.3"),sQuery(id+"F4.wireOp",EDGE,"E14.1.0.4"),sQuery(id+"F4.wireOp",EDGE,"E14.1.0.5"),sQuery(id+"F4.wireOp",EDGE,"E14.1.0.6"),sQuery(id+"F4.wireOp",EDGE,"E14.2.0.0"),sQuery(id+"F4.wireOp",EDGE,"E14.2.0.1"),sQuery(id+"F4.wireOp",EDGE,"E14.2.0.2"),sQuery(id+"F4.wireOp",EDGE,"E14.2.0.3"),sQuery(id+"F4.wireOp",EDGE,"E14.2.0.4"),sQuery(id+"F4.wireOp",EDGE,"E14.2.0.5"),sQuery(id+"F4.wireOp",EDGE,"E14.2.0.6"),sQuery(id+"F4.wireOp",EDGE,"E14.3.0.0"),sQuery(id+"F4.wireOp",EDGE,"E14.3.0.1"),sQuery(id+"F4.wireOp",EDGE,"E14.3.0.2"),sQuery(id+"F4.wireOp",EDGE,"E14.3.0.3"),sQuery(id+"F4.wireOp",EDGE,"E14.3.0.4"),sQuery(id+"F4.wireOp",EDGE,"E14.3.0.5"),sQuery(id+"F4.wireOp",EDGE,"E14.3.0.6"),sQuery(id+"F4.wireOp",EDGE,"E14.4.0.0"),sQuery(id+"F4.wireOp",EDGE,"E14.4.0.1"),sQuery(id+"F4.wireOp",EDGE,"E14.4.0.2"),sQuery(id+"F4.wireOp",EDGE,"E14.4.0.3"),sQuery(id+"F4.wireOp",EDGE,"E14.4.0.4"),sQuery(id+"F4.wireOp",EDGE,"E14.4.0.5"),sQuery(id+"F4.wireOp",EDGE,"E14.4.0.6"),sQuery(id+"F4.wireOp",EDGE,"E14.5.0.0"),sQuery(id+"F4.wireOp",EDGE,"E14.5.0.1"),sQuery(id+"F4.wireOp",EDGE,"E14.5.0.2"),sQuery(id+"F4.wireOp",EDGE,"E14.5.0.3"),sQuery(id+"F4.wireOp",EDGE,"E14.5.0.4"),sQuery(id+"F4.wireOp",EDGE,"E14.5.0.5"),sQuery(id+"F4.wireOp",EDGE,"E14.5.0.6"),sQuery(id+"F4.wireOp",EDGE,"E14.6.0.0"),sQuery(id+"F4.wireOp",EDGE,"E14.6.0.1"),sQuery(id+"F4.wireOp",EDGE,"E14.6.0.2"),sQuery(id+"F4.wireOp",EDGE,"E14.6.0.3"),sQuery(id+"F4.wireOp",EDGE,"E14.6.0.4"),sQuery(id+"F4.wireOp",EDGE,"E14.6.0.5"),sQuery(id+"F4.wireOp",EDGE,"E14.6.0.6"),sQuery(id+"F4.wireOp",EDGE,"E14.7.0.0"),sQuery(id+"F4.wireOp",EDGE,"E14.7.0.1"),sQuery(id+"F4.wireOp",EDGE,"E14.7.0.2"),sQuery(id+"F4.wireOp",EDGE,"E14.7.0.3"),sQuery(id+"F4.wireOp",EDGE,"E14.7.0.4"),sQuery(id+"F4.wireOp",EDGE,"E14.7.0.5"),sQuery(id+"F4.wireOp",EDGE,"E14.7.0.6"),sQuery(id+"F4.wireOp",EDGE,"E16.MirrorCS"),sQuery(id+"F4.wireOp",EDGE,"E17"),sQuery(id+"F4.wireOp",EDGE,"E18"),sQuery(id+"F4.wireOp",EDGE,"E22"),sQuery(id+"F4.wireOp",EDGE,"E23"),sQuery(id+"F4.wireOp",EDGE,"E24"),sQuery(id+"F4.wireOp",EDGE,"E25"),sQuery(id+"F4.wireOp",EDGE,"E26"),sQuery(id+"F4.wireOp",EDGE,"E27"),sQuery(id+"F4.wireOp",EDGE,"E28"),sQuery(id+"F4.wireOp",EDGE,"E29.4.8.0"),sQuery(id+"F4.wireOp",EDGE,"E29.8.8.0"),sQuery(id+"F4.wireOp",EDGE,"E29.12.8.0"),sQuery(id+"F4.wireOp",EDGE,"E29.22.8.0"),sQuery(id+"F4.wireOp",EDGE,"E30"),sQuery(id+"F4.wireOp",EDGE,"E40"),sQuery(id+"F4.wireOp",EDGE,"E42"),sQuery(id+"F4.wireOp",EDGE,"E43"),sQuery(id+"F4.wireOp",EDGE,"E48"),sQuery(id+"F4.wireOp",EDGE,"E49"),sQuery(id+"F4.wireOp",EDGE,"E51.0"),sQuery(id+"F4.wireOp",EDGE,"E51.1"),sQuery(id+"F4.wireOp",EDGE,"E52"),sQuery(id+"F4.wireOp",EDGE,"E53"),sQuery(id+"F4.wireOp",EDGE,"E54.filletArc"),sQuery(id+"F4.wireOp",EDGE,"E55.filletArc")])]});
            booleanBodies(context, id + "F11", {"operationType" : BooleanOperationType.SUBTRACTION, "tools" : qUnion([Q0]), "targets" : qUnion([Q1]), "keepTools" : true});
        }
        {
            var Q0;
            Q0=makeQuery(id+"F10.opExtrude","CAP_EDGE",EDGE,{"disambiguationData":[OSD([sQuery(id+"F4.wireOp",EDGE,"E45")])],"isStart":false});
            var Q1;
            Q1=makeQuery(id+"F10.opExtrude","CAP_EDGE",EDGE,{"disambiguationData":[OSD([sQuery(id+"F4.wireOp",EDGE,"E45")])],"isStart":true});
            var Q2;
            Q2=makeQuery(id+"F10.opExtrude","CAP_EDGE",EDGE,{"disambiguationData":[OSD([sQuery(id+"F4.wireOp",EDGE,"E46")])],"isStart":false});
            var Q3;
            Q3=makeQuery(id+"F10.opExtrude","CAP_EDGE",EDGE,{"disambiguationData":[OSD([sQuery(id+"F4.wireOp",EDGE,"E46")])],"isStart":true});
            var Q4;
            Q4=makeQuery(id+"F9.opExtrude","CAP_EDGE",EDGE,{"disambiguationData":[OSD([sQuery(id+"F4.wireOp",EDGE,"E47")])],"isStart":true});
            var Q5;
            Q5=makeQuery(id+"F9.opExtrude","CAP_EDGE",EDGE,{"disambiguationData":[OSD([sQuery(id+"F4.wireOp",EDGE,"E47")])],"isStart":false});
            var Q6;
            Q6=makeQuery(id+"F7.opExtrude","CAP_EDGE",EDGE,{"disambiguationData":[OSD([sQuery(id+"F4.wireOp",EDGE,"E49")])],"isStart":false});
            var Q7;
            Q7=makeQuery(id+"F7.opExtrude","CAP_EDGE",EDGE,{"disambiguationData":[OSD([sQuery(id+"F4.wireOp",EDGE,"E49")])],"isStart":true});
            fillet(context, id + "F12", {"entities" : qUnion([Q0, Q1, Q2, Q3, Q4, Q5, Q6, Q7]), "radius" : getVariable(context, 'vacChamberFillet') * 2 * mm, "tangentPropagation" : true, "allowEdgeOverflow" : false});
        }
    });
